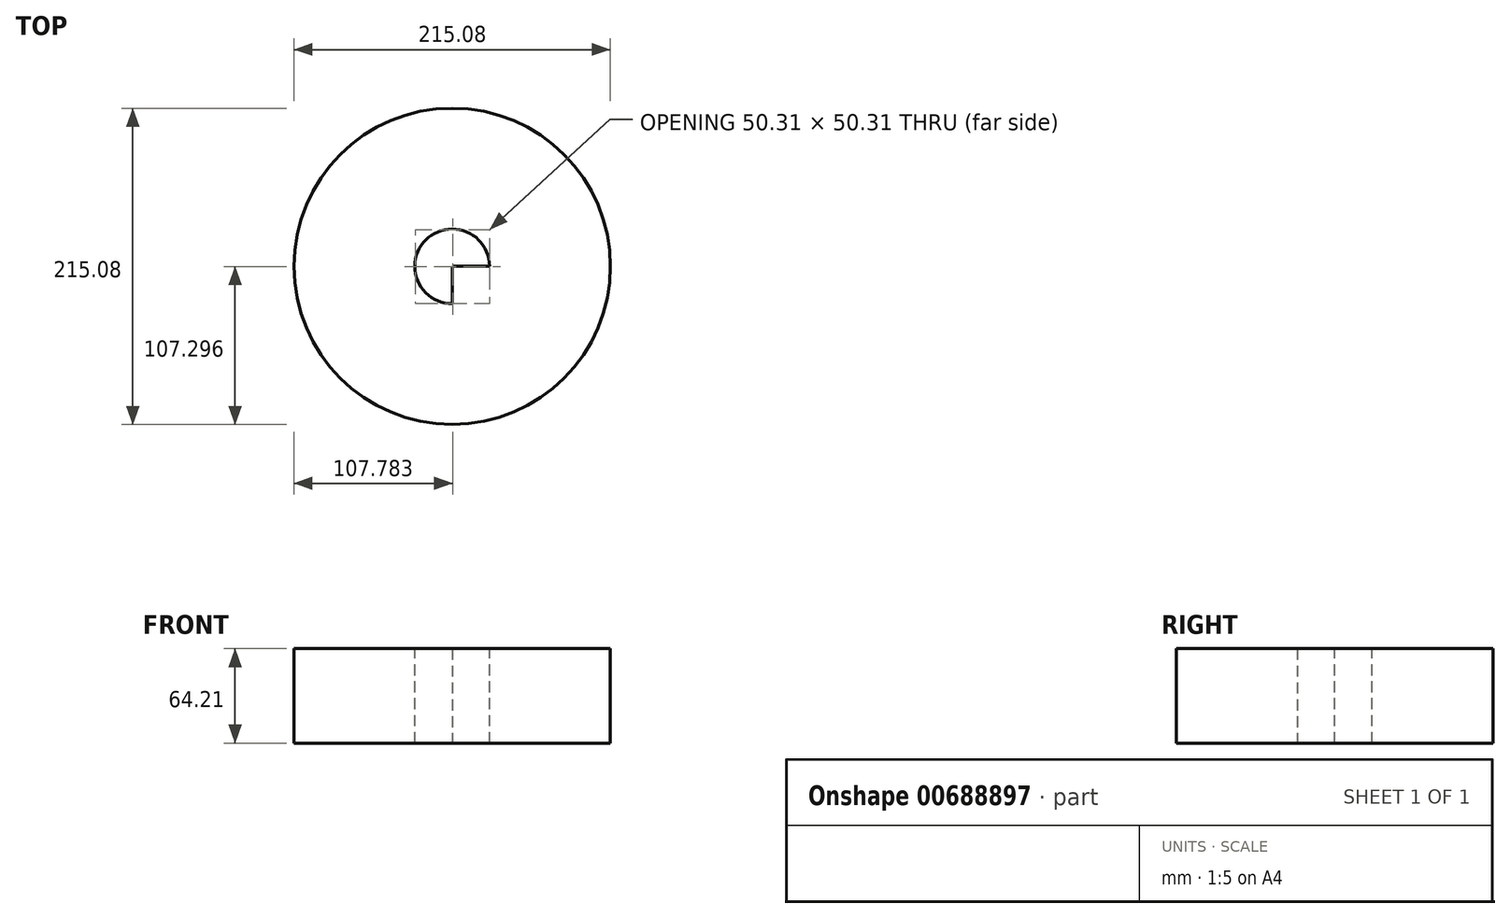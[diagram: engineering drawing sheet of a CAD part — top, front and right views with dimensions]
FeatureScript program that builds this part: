
annotation { "Feature Type Name" : "Feature", "Feature Type Description" : "" }
export const myFeature = defineFeature(function(context is Context, id is Id, definition is map)
    precondition{}
    {
        {
            var Q0;
            Q0=qCreatedBy(makeId("Front.planeOp"),FACE);
            var sketch = newSketch(context, id + "F0", { "sketchPlane" : qUnion([Q0])});
            skLineSegment(sketch, "E0.bottom", {"start": v(-48.94, 31.92) * mm, "end": v(55.55, 31.92) * mm});
            skLineSegment(sketch, "E0.top", {"start": v(-48.94, -32.3) * mm, "end": v(55.55, -32.3) * mm});
            skLineSegment(sketch, "E0.left", {"start": v(-48.94, 31.92) * mm, "end": v(-48.94, -32.3) * mm});
            skLineSegment(sketch, "E0.right", {"start": v(55.55, 31.92) * mm, "end": v(55.55, -32.3) * mm});
            skSolve(sketch);
        }
        {
            var Q0;
            Q0=makeQuery(id+"F0.imprint","IMPRINT",FACE,{"disambiguationData":[TD([[makeQuery(id+"F0.imprint","IMPRINT",EDGE,{"derivedFrom":sQuery(id+"F0.wireOp",EDGE,"E0.bottom")}),-1.0]])]});
            extrude(context, id + "F1", {"entities" : qUnion([Q0]), "depth" : 25.4 * mm, "offsetDistance" : 25.4 * mm});
        }
        {
            var Q0;
            Q0=makeQuery(id+"F1.opExtrude","CAP_FACE",FACE,{"disambiguationData":[OSD([sQuery(id+"F0.wireOp",EDGE,"E0.bottom"),sQuery(id+"F0.wireOp",EDGE,"E0.top"),sQuery(id+"F0.wireOp",EDGE,"E0.left"),sQuery(id+"F0.wireOp",EDGE,"E0.right")])],"isStart":false});
            var Q1;
            Q1=makeQuery(id+"F1.opExtrude","CAP_EDGE",EDGE,{"disambiguationData":[OSD([sQuery(id+"F0.wireOp",EDGE,"E0.left")])],"isStart":true});
            revolve(context, id + "F2", {"operationType" : NewBodyOperationType.ADD, "entities" : qUnion([Q0]), "axis" : qUnion([Q1]), "revolveType" : RevolveType.FULL});
        }
    });
